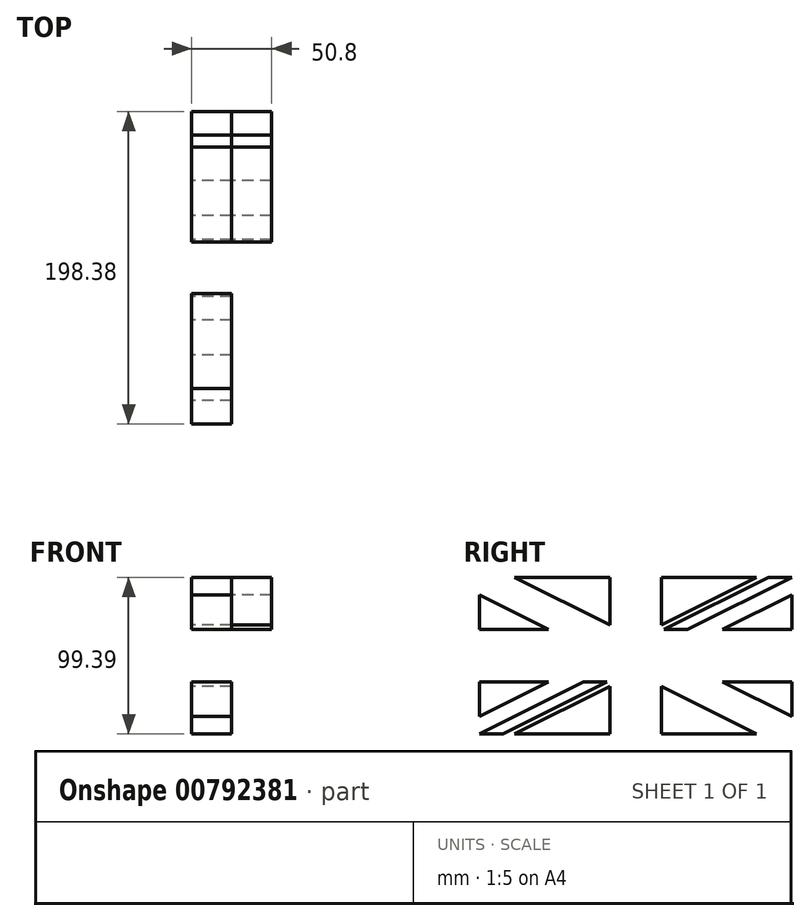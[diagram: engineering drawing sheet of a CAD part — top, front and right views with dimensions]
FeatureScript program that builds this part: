
annotation { "Feature Type Name" : "Feature", "Feature Type Description" : "" }
export const myFeature = defineFeature(function(context is Context, id is Id, definition is map)
    precondition{}
    {
        {
            var Q0;
            Q0=qCreatedBy(makeId("Right.planeOp"),FACE);
            var sketch = newSketch(context, id + "F0", { "sketchPlane" : qUnion([Q0])});
            skLineSegment(sketch, "E0", {"start": v(55.31, 10.95) * mm, "end": v(99.19, 10.95) * mm});
            skLineSegment(sketch, "E1", {"start": v(99.19, 10.95) * mm, "end": v(99.19, 32.78) * mm});
            skLineSegment(sketch, "E2", {"start": v(99.19, 32.78) * mm, "end": v(55.31, 10.95) * mm});
            skLineSegment(sketch, "E3", {"start": v(33.04, 10.83) * mm, "end": v(18.1, 10.83) * mm});
            skLineSegment(sketch, "E4", {"start": v(18.1, 10.83) * mm, "end": v(84.33, 43.96) * mm});
            skLineSegment(sketch, "E5", {"start": v(84.33, 43.96) * mm, "end": v(99.19, 43.96) * mm});
            skLineSegment(sketch, "E6", {"start": v(99.19, 43.96) * mm, "end": v(33.04, 10.83) * mm});
            skLineSegment(sketch, "E7", {"start": v(16.4, 13.8) * mm, "end": v(16.4, 43.96) * mm});
            skLineSegment(sketch, "E8", {"start": v(16.4, 43.96) * mm, "end": v(76.74, 43.96) * mm});
            skLineSegment(sketch, "E9", {"start": v(76.74, 43.96) * mm, "end": v(16.4, 13.8) * mm});
            skLineSegment(sketch, "E10", {"start": v(99.19, -5.73) * mm, "end": v(-99.58, -5.73) * mm, "construction": true});
            skLineSegment(sketch, "E11", {"start": v(0, 43.96) * mm, "end": v(0, -55.43) * mm, "construction": true});
            skLineSegment(sketch, "E12.MirrorCS", {"start": v(-99.19, -5.73) * mm, "end": v(99.58, -5.73) * mm, "construction": true});
            skLineSegment(sketch, "E13.MirrorCS", {"start": v(-16.4, 43.96) * mm, "end": v(-76.74, 43.96) * mm});
            skLineSegment(sketch, "E14.MirrorCS", {"start": v(-99.19, 43.96) * mm, "end": v(-33.04, 10.83) * mm});
            skLineSegment(sketch, "E15.MirrorCS", {"start": v(-33.04, 10.83) * mm, "end": v(-18.1, 10.83) * mm});
            skLineSegment(sketch, "E16.MirrorCS", {"start": v(-18.1, 10.83) * mm, "end": v(-84.33, 43.96) * mm});
            skLineSegment(sketch, "E17.MirrorCS", {"start": v(-84.33, 43.96) * mm, "end": v(-99.19, 43.96) * mm});
            skLineSegment(sketch, "E18.MirrorCS", {"start": v(-76.74, 43.96) * mm, "end": v(-16.4, 13.8) * mm});
            skLineSegment(sketch, "E19.MirrorCS", {"start": v(-16.4, 13.8) * mm, "end": v(-16.4, 43.96) * mm});
            skLineSegment(sketch, "E20.MirrorCS", {"start": v(-99.19, 32.78) * mm, "end": v(-55.31, 10.95) * mm});
            skLineSegment(sketch, "E21.MirrorCS", {"start": v(-55.31, 10.95) * mm, "end": v(-99.19, 10.95) * mm});
            skLineSegment(sketch, "E22.MirrorCS", {"start": v(-99.19, 10.95) * mm, "end": v(-99.19, 32.78) * mm});
            skLineSegment(sketch, "E23.MirrorCS", {"start": v(-55.31, -22.42) * mm, "end": v(-99.19, -22.42) * mm});
            skLineSegment(sketch, "E24.MirrorCS", {"start": v(-99.19, -22.42) * mm, "end": v(-99.19, -44.25) * mm});
            skLineSegment(sketch, "E25.MirrorCS", {"start": v(-99.19, -44.25) * mm, "end": v(-55.31, -22.42) * mm});
            skLineSegment(sketch, "E26.MirrorCS", {"start": v(-16.4, -55.43) * mm, "end": v(-76.74, -55.43) * mm});
            skLineSegment(sketch, "E27.MirrorCS", {"start": v(-16.4, -25.26) * mm, "end": v(-16.4, -55.43) * mm});
            skLineSegment(sketch, "E28.MirrorCS", {"start": v(-76.74, -55.43) * mm, "end": v(-16.4, -25.26) * mm});
            skLineSegment(sketch, "E29.MirrorCS", {"start": v(-84.33, -55.43) * mm, "end": v(-99.19, -55.43) * mm});
            skLineSegment(sketch, "E30.MirrorCS", {"start": v(-33.04, -22.3) * mm, "end": v(-18.1, -22.3) * mm});
            skLineSegment(sketch, "E31.MirrorCS", {"start": v(-99.19, -55.43) * mm, "end": v(-33.04, -22.3) * mm});
            skLineSegment(sketch, "E32.MirrorCS", {"start": v(-18.1, -22.3) * mm, "end": v(-84.33, -55.43) * mm});
            skLineSegment(sketch, "E33.MirrorCS", {"start": v(16.4, -25.26) * mm, "end": v(16.4, -55.43) * mm});
            skLineSegment(sketch, "E34.MirrorCS", {"start": v(76.74, -55.43) * mm, "end": v(16.4, -25.26) * mm});
            skLineSegment(sketch, "E35.MirrorCS", {"start": v(18.1, -22.3) * mm, "end": v(84.33, -55.43) * mm});
            skLineSegment(sketch, "E36.MirrorCS", {"start": v(99.19, -55.43) * mm, "end": v(33.04, -22.3) * mm});
            skLineSegment(sketch, "E37.MirrorCS", {"start": v(33.04, -22.3) * mm, "end": v(18.1, -22.3) * mm});
            skLineSegment(sketch, "E38.MirrorCS", {"start": v(99.19, -44.25) * mm, "end": v(55.31, -22.42) * mm});
            skLineSegment(sketch, "E39.MirrorCS", {"start": v(55.31, -22.42) * mm, "end": v(99.19, -22.42) * mm});
            skLineSegment(sketch, "E40.MirrorCS", {"start": v(99.19, -22.42) * mm, "end": v(99.19, -44.25) * mm});
            skLineSegment(sketch, "E41.MirrorCS", {"start": v(84.33, -55.43) * mm, "end": v(99.19, -55.43) * mm});
            skLineSegment(sketch, "E42.MirrorCS", {"start": v(16.4, -55.43) * mm, "end": v(76.74, -55.43) * mm});
            skSolve(sketch);
        }
        {
            var Q0;
            Q0=makeQuery(id+"F0.imprint","IMPRINT",FACE,{"disambiguationData":[TD([[makeQuery(id+"F0.imprint","IMPRINT",EDGE,{"derivedFrom":sQuery(id+"F0.wireOp",EDGE,"E0")}),1.0]])]});
            extrude(context, id + "F1", {"entities" : qUnion([Q0]), "depth" : 25.4 * mm, "offsetDistance" : 25.4 * mm});
        }
        {
            var Q0;
            Q0=makeQuery(id+"F0.imprint","IMPRINT",FACE,{"disambiguationData":[TD([[makeQuery(id+"F0.imprint","IMPRINT",EDGE,{"derivedFrom":sQuery(id+"F0.wireOp",EDGE,"E3")}),-1.0]])]});
            extrude(context, id + "F2", {"entities" : qUnion([Q0]), "depth" : 25.4 * mm, "offsetDistance" : 25.4 * mm});
        }
        {
            var Q0;
            Q0=makeQuery(id+"F0.imprint","IMPRINT",FACE,{"disambiguationData":[TD([[makeQuery(id+"F0.imprint","IMPRINT",EDGE,{"derivedFrom":sQuery(id+"F0.wireOp",EDGE,"E7")}),-1.0]])]});
            extrude(context, id + "F3", {"entities" : qUnion([Q0]), "depth" : 25.4 * mm, "offsetDistance" : 25.4 * mm});
        }
        {
            var Q0;
            Q0=makeQuery(id+"F0.imprint","IMPRINT",FACE,{"disambiguationData":[TD([[makeQuery(id+"F0.imprint","IMPRINT",EDGE,{"derivedFrom":sQuery(id+"F0.wireOp",EDGE,"E26.MirrorCS")}),-1.0]])]});
            var Q1;
            Q1=makeQuery(id+"F0.imprint","IMPRINT",FACE,{"disambiguationData":[TD([[makeQuery(id+"F0.imprint","IMPRINT",EDGE,{"derivedFrom":sQuery(id+"F0.wireOp",EDGE,"E29.MirrorCS")}),-1.0]])]});
            var Q2;
            Q2=makeQuery(id+"F0.imprint","IMPRINT",FACE,{"disambiguationData":[TD([[makeQuery(id+"F0.imprint","IMPRINT",EDGE,{"derivedFrom":sQuery(id+"F0.wireOp",EDGE,"E23.MirrorCS")}),1.0]])]});
            var Q3;
            Q3=makeQuery(id+"F0.imprint","IMPRINT",FACE,{"disambiguationData":[TD([[makeQuery(id+"F0.imprint","IMPRINT",EDGE,{"derivedFrom":sQuery(id+"F0.wireOp",EDGE,"E33.MirrorCS")}),1.0]])]});
            var Q4;
            Q4=makeQuery(id+"F0.imprint","IMPRINT",FACE,{"disambiguationData":[TD([[makeQuery(id+"F0.imprint","IMPRINT",EDGE,{"derivedFrom":sQuery(id+"F0.wireOp",EDGE,"E38.MirrorCS")}),-1.0]])]});
            var Q5;
            Q5=makeQuery(id+"F1.opExtrude","CAP_FACE",FACE,{"disambiguationData":[OSD([sQuery(id+"F0.wireOp",EDGE,"E0"),sQuery(id+"F0.wireOp",EDGE,"E1"),sQuery(id+"F0.wireOp",EDGE,"E2")])],"isStart":false});
            var Q6;
            Q6=makeQuery(id+"F3.opExtrude","CAP_FACE",FACE,{"disambiguationData":[OSD([sQuery(id+"F0.wireOp",EDGE,"E7"),sQuery(id+"F0.wireOp",EDGE,"E8"),sQuery(id+"F0.wireOp",EDGE,"E9")])],"isStart":false});
            var Q7;
            Q7=makeQuery(id+"F2.opExtrude","CAP_FACE",FACE,{"disambiguationData":[OSD([sQuery(id+"F0.wireOp",EDGE,"E3"),sQuery(id+"F0.wireOp",EDGE,"E5"),sQuery(id+"F0.wireOp",EDGE,"E6"),sQuery(id+"F0.wireOp",EDGE,"E4")])],"isStart":false});
            var Q8;
            Q8=makeQuery(id+"F0.imprint","IMPRINT",FACE,{"disambiguationData":[TD([[makeQuery(id+"F0.imprint","IMPRINT",EDGE,{"derivedFrom":sQuery(id+"F0.wireOp",EDGE,"E18.MirrorCS")}),1.0]])]});
            var Q9;
            Q9=makeQuery(id+"F0.imprint","IMPRINT",FACE,{"disambiguationData":[TD([[makeQuery(id+"F0.imprint","IMPRINT",EDGE,{"derivedFrom":sQuery(id+"F0.wireOp",EDGE,"E20.MirrorCS")}),-1.0]])]});
            extrude(context, id + "F4", {"entities" : qUnion([Q0, Q1, Q2, Q3, Q4, Q5, Q6, Q7, Q8, Q9]), "depth" : 25.4 * mm, "offsetDistance" : 25.4 * mm});
        }
    });
